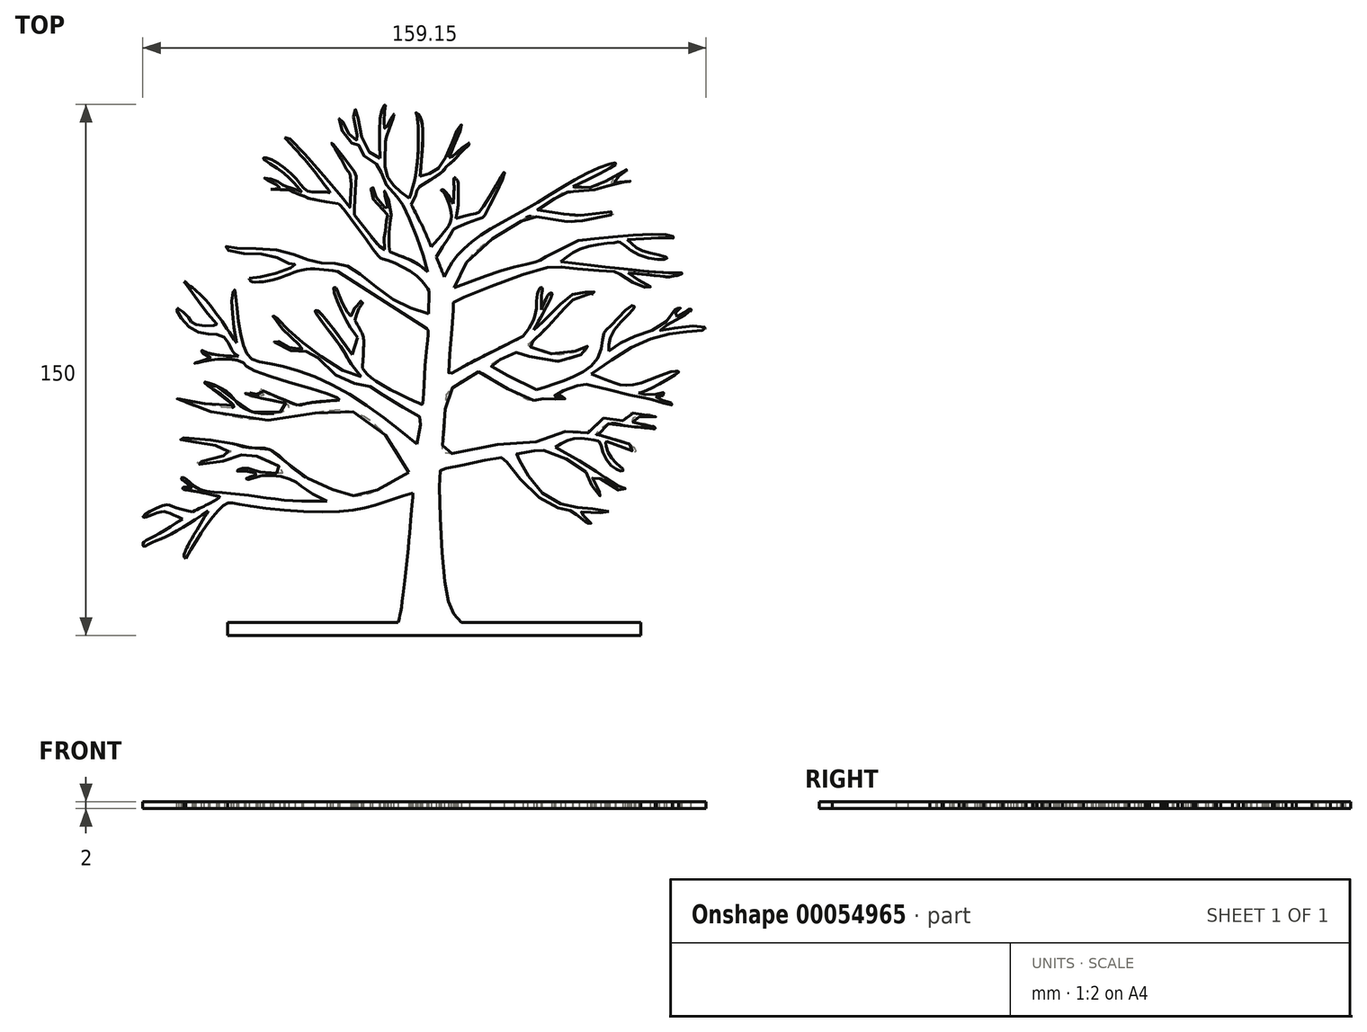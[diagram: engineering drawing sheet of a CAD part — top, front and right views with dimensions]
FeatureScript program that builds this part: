
annotation { "Feature Type Name" : "Feature", "Feature Type Description" : "" }
export const myFeature = defineFeature(function(context is Context, id is Id, definition is map)
    precondition{}
    {
        {
            var Q0;
            Q0=qCreatedBy(makeId("Top.planeOp"),FACE);
            var sketch = newSketch(context, id + "F0", { "sketchPlane" : qUnion([Q0])});
            skFitSpline(sketch, "E0", {"points": [v(-10.21, -68.81) * mm, v(-9.37, -65.06) * mm, v(-6.85, -42.52) * mm, v(-6.02, -32.17) * mm], "startDerivative": vector(3.97, 13.71) * mm, "endDerivative": vector(1.9, 26.28) * mm});
            skFitSpline(sketch, "E1", {"points": [v(-6.02, -32.17) * mm, v(-14.74, -35.01) * mm, v(-27.66, -37.49) * mm, v(-54.51, -35.53) * mm, v(-58.1, -35.01) * mm, v(-60.6, -36.76) * mm, v(-65.35, -42.8) * mm, v(-70.21, -50.73) * mm], "startDerivative": vector(-61.25, -20.1) * mm, "endDerivative": vector(-32.79, -56.2) * mm});
            skFitSpline(sketch, "E2", {"points": [v(-70.21, -50.73) * mm, v(-70.69, -50.15) * mm, v(-63.82, -37.26) * mm], "startDerivative": vector(-3.59, 1.97) * mm, "endDerivative": vector(12.9, 20.96) * mm});
            skFitSpline(sketch, "E3", {"points": [v(-63.82, -37.26) * mm, v(-74.43, -43.86) * mm, v(-80.19, -46.45) * mm, v(-82.14, -47.24) * mm, v(-82.25, -46.4) * mm, v(-79.66, -44.7) * mm, v(-71.1, -39.59) * mm], "startDerivative": vector(-42.12, -28.38) * mm, "endDerivative": vector(39.65, 25.02) * mm});
            skFitSpline(sketch, "E4", {"points": [v(-71.1, -39.59) * mm, v(-75.12, -37.8) * mm, v(-76.86, -37.53) * mm, v(-80.61, -38.69) * mm, v(-81.77, -39.11) * mm, v(-82.25, -38.9) * mm, v(-76.18, -35.63) * mm, v(-73.96, -36.05) * mm, v(-68.31, -37.53) * mm], "startDerivative": vector(-29.89, 13.9) * mm, "endDerivative": vector(37.9, -8.18) * mm});
            skFitSpline(sketch, "E5", {"points": [v(-68.31, -37.53) * mm, v(-60.65, -33.25) * mm, v(-61.34, -33.04) * mm], "startDerivative": vector(14.87, 7.27) * mm, "endDerivative": vector(-4.52, 0.44) * mm});
            skFitSpline(sketch, "E6", {"points": [v(-61.34, -33.04) * mm, v(-67.57, -31.72) * mm, v(-70.95, -31.2) * mm], "startDerivative": vector(-11.6, 2.59) * mm, "endDerivative": vector(-7.4, 1.03) * mm});
            skFitSpline(sketch, "E7", {"points": [v(-70.95, -31.2) * mm, v(-70.95, -30.66) * mm, v(-68.42, -30.77) * mm], "startDerivative": vector(-0.58, 1.97) * mm, "endDerivative": vector(4.96, -0.79) * mm});
            skFitSpline(sketch, "E8", {"points": [v(-68.42, -30.77) * mm, v(-71.4, -27.91) * mm, v(-70.6, -27.87) * mm, v(-67.1, -30.77) * mm, v(-56.96, -32.35) * mm, v(-43.07, -34.15) * mm, v(-30.3, -34.57) * mm], "startDerivative": vector(-35.84, 33.17) * mm, "endDerivative": vector(52.6, 0.18) * mm});
            skFitSpline(sketch, "E9", {"points": [v(-30.3, -34.57) * mm, v(-36.13, -31.33) * mm, v(-39.86, -28.69) * mm, v(-48.85, -27.33) * mm, v(-52.94, -28.36) * mm, v(-53.06, -28.02) * mm, v(-50.3, -27.02) * mm, v(-53.27, -26.05) * mm, v(-55.7, -26.01) * mm, v(-55.45, -25.72) * mm, v(-53.14, -25.22) * mm, v(-49.27, -26.31) * mm], "startDerivative": vector(-47.94, 23.7) * mm, "endDerivative": vector(38.86, -13.3) * mm});
            skFitSpline(sketch, "E10", {"points": [v(-49.27, -26.31) * mm, v(-46.74, -26.35) * mm, v(-42.38, -26.31) * mm, v(-47.57, -22.53) * mm, v(-51.93, -21.7) * mm, v(-55.12, -21.53) * mm, v(-60.48, -23.41) * mm, v(-66.93, -24.04) * mm, v(-67.27, -23.8) * mm, v(-66.77, -23.5) * mm, v(-61.57, -22.4) * mm, v(-57.34, -20.48) * mm, v(-58.1, -20.4) * mm, v(-59.14, -19.9) * mm, v(-62.91, -18.47) * mm, v(-68.06, -17.84) * mm, v(-71.33, -17.25) * mm, v(-72.09, -16.88) * mm, v(-72, -16.46) * mm, v(-71.12, -16.5) * mm, v(-61.74, -17.34) * mm, v(-56.29, -18.47) * mm, v(-51.89, -19.43) * mm, v(-46.57, -19.9) * mm, v(-41.83, -23.54) * mm, v(-34.08, -28.99) * mm, v(-25.83, -32.17) * mm, v(-20.38, -32.89) * mm, v(-7.18, -26.34) * mm], "startDerivative": vector(66.46, 23.55) * mm, "endDerivative": vector(214.35, 130.31) * mm});
            skFitSpline(sketch, "E11", {"points": [v(-7.18, -26.34) * mm, v(-23.22, -9.2) * mm, v(-50.68, -11.54) * mm, v(-72.4, -5.4) * mm, v(-56.58, -7.78) * mm, v(-64.95, -1) * mm, v(-58.66, -3.55) * mm, v(-55.26, -7.18) * mm, v(-47.65, -9.86) * mm, v(-40.93, -7.9) * mm, v(-46.68, -5.65) * mm, v(-52.16, -4.92) * mm, v(-53.51, -3.83) * mm, v(-50.42, -4.28) * mm, v(-48.15, -4.43) * mm, v(-49.1, -3.6) * mm, v(-49.67, -2.48) * mm, v(-46.75, -4.28) * mm, v(-42.82, -5.7) * mm, v(-38.61, -7.37) * mm, v(-36.22, -6.94) * mm, v(-26.74, -6) * mm], "startDerivative": vector(-116.92, 253.36) * mm, "endDerivative": vector(202.88, 11.26) * mm});
            skFitSpline(sketch, "E12", {"points": [v(-26.74, -6) * mm, v(-27.4, -5.29) * mm, v(-51.95, 2.9) * mm, v(-54.07, 4.7) * mm, v(-60.8, 5.62) * mm, v(-67.64, 4.5) * mm, v(-63.32, 6.09) * mm, v(-64.92, 6.89) * mm, v(-65.71, 8.02) * mm, v(-64.38, 7.49) * mm, v(-55.34, 6.35) * mm], "startDerivative": vector(-3.14, 13.4) * mm, "endDerivative": vector(77.7, -4.3) * mm});
            skFitSpline(sketch, "E13", {"points": [v(-55.34, 6.35) * mm, v(-56.87, 7.68) * mm, v(-59.8, 12.08) * mm, v(-67.84, 13.74) * mm, v(-72.7, 20) * mm, v(-69.57, 17.53) * mm, v(-67.64, 15.47) * mm, v(-61.52, 15.33) * mm, v(-61.99, 16.13) * mm, v(-70.7, 27.64) * mm], "startDerivative": vector(-22.53, 12.79) * mm, "endDerivative": vector(-57, 78.87) * mm});
            skFitSpline(sketch, "E14", {"points": [v(-70.7, 27.64) * mm, v(-64.72, 22.45) * mm, v(-55.87, 10.21) * mm], "startDerivative": vector(14.04, -10.51) * mm, "endDerivative": vector(15.55, -23.64) * mm});
            skFitSpline(sketch, "E15", {"points": [v(-55.87, 10.21) * mm, v(-57.13, 22.92) * mm, v(-56.47, 25.31) * mm, v(-55.87, 21.12) * mm, v(-54.07, 10.21) * mm, v(-51.75, 5.82) * mm, v(-46.56, 4.36) * mm, v(-29, -1.5) * mm, v(-4.85, -18.32) * mm], "startDerivative": vector(-16.04, 99.74) * mm, "endDerivative": vector(109.24, -87.43) * mm});
            skFitSpline(sketch, "E16", {"points": [v(-4.85, -18.32) * mm, v(-3.65, -11.34) * mm, v(-3.92, -10.8) * mm, v(-13.16, -5.49) * mm, v(-18.62, -1.96) * mm, v(-26.2, 0) * mm, v(-35.07, 7.69) * mm, v(-38.26, 7.49) * mm, v(-45.3, 10.68) * mm, v(-44.51, 10.88) * mm, v(-43.51, 10.28) * mm, v(-39.06, 8.35) * mm, v(-36.93, 8.69) * mm, v(-37.93, 9.48) * mm, v(-45.3, 17.17) * mm, v(-45.5, 17.97) * mm, v(-44.44, 17.17) * mm, v(-40.63, 13.31) * mm, v(-31.61, 6.16) * mm, v(-20.61, 0.7) * mm], "startDerivative": vector(23.47, 124.9) * mm, "endDerivative": vector(98.14, 5.97) * mm});
            skFitSpline(sketch, "E17", {"points": [v(-20.61, 0.7) * mm, v(-24.2, 5.42) * mm, v(-26, 8.55) * mm, v(-33.59, 18.93) * mm, v(-33.59, 19.33) * mm, v(-32.99, 19.26) * mm, v(-23.14, 6.89) * mm], "startDerivative": vector(-23.28, 28.66) * mm, "endDerivative": vector(41.77, -57.86) * mm});
            skFitSpline(sketch, "E18", {"points": [v(-23.14, 6.89) * mm, v(-21.61, 11.68) * mm], "startDerivative": vector(1.53, 4.79) * mm, "endDerivative": vector(1.53, 4.79) * mm});
            skFitSpline(sketch, "E19", {"points": [v(-21.61, 11.68) * mm, v(-25, 16.86) * mm, v(-28.4, 25.84) * mm, v(-27.8, 25.84) * mm, v(-27.27, 24.65) * mm, v(-23.54, 17.86) * mm, v(-22.63, 19.86) * mm, v(-21.61, 20.79) * mm, v(-20.81, 22.05) * mm, v(-20.22, 21.52) * mm, v(-20.81, 20.66) * mm, v(-22.42, 16.53) * mm], "startDerivative": vector(-22.32, 29) * mm, "endDerivative": vector(-12.72, -43.1) * mm});
            skFitSpline(sketch, "E20", {"points": [v(-22.42, 16.53) * mm, v(-20.31, 12.68) * mm, v(-19.93, 10.55) * mm, v(-20.31, 3.05) * mm], "startDerivative": vector(7.63, -12.78) * mm, "endDerivative": vector(-1.42, -20.17) * mm});
            skFitSpline(sketch, "E21", {"points": [v(-20.31, 3.05) * mm, v(-16.12, -0.8) * mm, v(-3.6, -7.13) * mm, v(-3.26, -6.96) * mm, v(-2.25, 7.83) * mm, v(-2.12, 14.29) * mm], "startDerivative": vector(15.8, -20) * mm, "endDerivative": vector(-12.14, 4.1) * mm});
            skFitSpline(sketch, "E22", {"points": [v(-52.28, 28.5) * mm, v(-48.13, 28.97) * mm, v(-40.94, 31.23) * mm, v(-39.2, 32.07) * mm, v(-39.65, 32.56) * mm, v(-40.85, 32.6) * mm, v(-45.69, 34.83) * mm, v(-54.03, 35.45) * mm, v(-59, 36.87) * mm, v(-59, 37.4) * mm, v(-56.52, 37.05) * mm, v(-45.24, 36.6) * mm, v(-37.07, 34.2) * mm, v(-31.48, 32.78) * mm, v(-26.33, 32.52) * mm, v(-21.27, 29.94) * mm, v(-11.5, 22.48) * mm, v(-1.65, 18.49) * mm], "startDerivative": vector(66.06, 8.87) * mm, "endDerivative": vector(114.77, -35.11) * mm});
            skLineSegment(sketch, "E23", {"start": v(-10.21, -68.81) * mm, "end": v(7.61, -68.81) * mm});
            skLineSegment(sketch, "E24", {"start": v(-27.3, 30.4) * mm, "end": v(-2.12, 14.29) * mm});
            skFitSpline(sketch, "E25", {"points": [v(-1.65, 18.49) * mm, v(-1.45, 24.39) * mm, v(-1.47, 24.8) * mm, v(-1.82, 25.43) * mm, v(-5.7, 29.72) * mm, v(-14.62, 34.02) * mm, v(-15.6, 34.58) * mm, v(-26.86, 49.48) * mm, v(-27.16, 49.55) * mm], "startDerivative": vector(1.62, 48.58) * mm, "endDerivative": vector(-5.15, -2.9) * mm});
            skFitSpline(sketch, "E26", {"points": [v(-27.16, 49.55) * mm, v(-35.09, 50.95) * mm, v(-35.73, 51.15) * mm, v(-36.52, 51.58) * mm, v(-37.54, 51.94) * mm, v(-40.76, 53.37) * mm, v(-41.14, 53.43) * mm, v(-46.15, 53.65) * mm, v(-43.56, 54.09) * mm, v(-47.97, 56.7) * mm, v(-44.87, 56.11) * mm, v(-42.36, 54.6) * mm, v(-40.3, 54.03) * mm, v(-37.47, 52.89) * mm], "startDerivative": vector(-75.54, 13.06) * mm, "endDerivative": vector(34.7, -16.07) * mm});
            skFitSpline(sketch, "E27", {"points": [v(-37.47, 52.89) * mm, v(-38.58, 54.3) * mm, v(-43.27, 58.75) * mm, v(-48.28, 62.44) * mm, v(-46.15, 62.04) * mm, v(-38.77, 56.35) * mm, v(-35.76, 53.08) * mm, v(-32.15, 52.89) * mm, v(-29.37, 52.65) * mm], "startDerivative": vector(-11.68, 15.44) * mm, "endDerivative": vector(25.9, -3.8) * mm});
            skFitSpline(sketch, "E28", {"points": [v(-29.37, 52.65) * mm, v(-34.96, 60.06) * mm, v(-42.23, 68.23) * mm], "startDerivative": vector(-11.1, 15.38) * mm, "endDerivative": vector(-14.57, 15.77) * mm});
            skFitSpline(sketch, "E29", {"points": [v(-42.23, 68.23) * mm, v(-41.28, 68.23) * mm, v(-23.87, 48.52) * mm, v(-23.83, 48.48) * mm, v(-23.61, 57.44) * mm, v(-24.36, 58.75) * mm, v(-27.67, 64.62) * mm, v(-29.03, 66.72) * mm, v(-29.13, 67.02) * mm, v(-22.16, 58.1) * mm, v(-22, 57.64) * mm, v(-22.6, 46.71) * mm, v(-22.5, 46.36) * mm, v(-16.09, 38.18) * mm, v(-14.08, 36.58) * mm], "startDerivative": vector(16.33, 15.47) * mm, "endDerivative": vector(27.04, -14.44) * mm});
            skFitSpline(sketch, "E30", {"points": [v(-27.3, 30.4) * mm, v(-36.46, 30.94) * mm, v(-44.8, 28.26) * mm, v(-51.7, 27.62) * mm, v(-52.28, 28.5) * mm], "startDerivative": vector(-30.11, 4.82) * mm, "endDerivative": vector(-2.56, 9.45) * mm});
            skFitSpline(sketch, "E31", {"points": [v(-14.08, 36.58) * mm, v(-14.08, 40.86) * mm, v(-13.72, 42.16) * mm, v(-13.38, 46) * mm, v(-13.17, 46.35) * mm, v(-13.87, 47.23) * mm, v(-17.94, 52.2) * mm, v(-17.5, 54.38) * mm, v(-17.33, 54.38) * mm, v(-17.18, 52.9) * mm, v(-13.47, 48.07) * mm, v(-13.13, 47.99) * mm, v(-13.97, 51.83) * mm, v(-14.14, 53.21) * mm, v(-13.4, 52.17) * mm, v(-12.13, 45.8) * mm, v(-12.28, 45.5) * mm, v(-12.84, 40.36) * mm, v(-12.7, 36.1) * mm, v(-12.56, 35.96) * mm, v(-10.52, 35.13) * mm, v(-5.24, 32.9) * mm, v(-1.89, 30.28) * mm], "startDerivative": vector(-4.06, 81.98) * mm, "endDerivative": vector(47.57, -44.67) * mm});
            skFitSpline(sketch, "E32", {"points": [v(-1.89, 30.28) * mm, v(-4.65, 39.4) * mm, v(-8.63, 48.68) * mm, v(-10.13, 51.04) * mm, v(-14.63, 56.78) * mm, v(-15.3, 59.78) * mm, v(-20.1, 63.44) * mm, v(-21.47, 66.3) * mm, v(-23.5, 66.84) * mm, v(-26.9, 72.73) * mm, v(-26.6, 73.85) * mm, v(-25.53, 71.96) * mm, v(-22.8, 67.9) * mm, v(-21.63, 67.53) * mm, v(-21.71, 68.52) * mm, v(-22.81, 76.02) * mm, v(-22.29, 76.23) * mm, v(-21.77, 75) * mm, v(-19.33, 65.4) * mm, v(-15.26, 62.42) * mm], "startDerivative": vector(-28.5, 105.1) * mm, "endDerivative": vector(75.49, -28.96) * mm});
            skFitSpline(sketch, "E33", {"points": [v(-15.26, 62.42) * mm, v(-14.8, 76.02) * mm, v(-13.84, 77.57) * mm, v(-13.96, 76.02) * mm, v(-13.84, 70.71) * mm, v(-11.7, 74.6) * mm, v(-11.33, 74.77) * mm, v(-13.66, 68.03) * mm, v(-13.78, 66.48) * mm, v(-13.48, 58.01) * mm, v(-7.04, 51.1) * mm], "startDerivative": vector(-3.61, 94.5) * mm, "endDerivative": vector(56.5, -39.34) * mm});
            skFitSpline(sketch, "E34", {"points": [v(-7.04, 51.1) * mm, v(-4.83, 60.75) * mm, v(-5, 74.95) * mm, v(-5.19, 75.3) * mm, v(-4.06, 74.23) * mm, v(-4.06, 57.35) * mm], "startDerivative": vector(10.87, 32.93) * mm, "endDerivative": vector(-6.74, -67.77) * mm});
            skFitSpline(sketch, "E35", {"points": [v(-4.06, 57.35) * mm, v(1.79, 60.22) * mm, v(6.92, 71.13) * mm, v(7.81, 71.73) * mm, v(4.24, 62.54) * mm, v(4.47, 62.36) * mm, v(9.66, 66.72) * mm, v(10.02, 66.48) * mm, v(9.07, 65.59) * mm, v(4.3, 60.75) * mm, v(3.7, 60.52) * mm, v(2.62, 58.9) * mm, v(-4.77, 53.78) * mm, v(-4.9, 53.06) * mm, v(-6.5, 49.3) * mm], "startDerivative": vector(63.62, 11.93) * mm, "endDerivative": vector(-30.11, -58.53) * mm});
            skFitSpline(sketch, "E36", {"points": [v(-6.5, 49.3) * mm, v(-3.13, 42.64) * mm, v(-0.87, 37.38) * mm], "startDerivative": vector(6.73, -12.83) * mm, "endDerivative": vector(4.48, -10.98) * mm});
            skFitSpline(sketch, "E37", {"points": [v(-0.87, 37.38) * mm, v(3.94, 43.16) * mm, v(4.76, 47.22) * mm, v(2.43, 53) * mm, v(1.98, 53.3) * mm, v(2.36, 53.53) * mm, v(5.37, 49.55) * mm], "startDerivative": vector(22.46, 24.31) * mm, "endDerivative": vector(16.88, -28.84) * mm});
            skFitSpline(sketch, "E38", {"points": [v(5.37, 49.55) * mm, v(5.58, 54.8) * mm, v(5.7, 56.93) * mm, v(6.7, 55.86) * mm], "startDerivative": vector(0.83, 11.66) * mm, "endDerivative": vector(5.05, -6.97) * mm});
            skFitSpline(sketch, "E39", {"points": [v(6.7, 55.86) * mm, v(6.7, 48.85) * mm, v(6.09, 45.33) * mm], "startDerivative": vector(0.43, -13.05) * mm, "endDerivative": vector(-1.8, -7.7) * mm});
            skFitSpline(sketch, "E40", {"points": [v(6.09, 45.33) * mm, v(11.44, 46.77) * mm, v(12.99, 47.61) * mm, v(19.32, 58) * mm, v(19.68, 58.42) * mm, v(19.88, 58.3) * mm, v(13.94, 45.78) * mm, v(13.55, 45.59) * mm, v(5.64, 42.46) * mm, v(5.33, 42.12) * mm, v(0.56, 34.5) * mm], "startDerivative": vector(52.36, 15.08) * mm, "endDerivative": vector(-42.77, -66.51) * mm});
            skFitSpline(sketch, "E41", {"points": [v(0.56, 34.5) * mm, v(2.1, 30.73) * mm, v(2.82, 28.92) * mm], "startDerivative": vector(2.86, -6.96) * mm, "endDerivative": vector(1.58, -4.02) * mm});
            skFitSpline(sketch, "E42", {"points": [v(2.82, 28.92) * mm, v(6.1, 34.4) * mm, v(13.66, 41.04) * mm, v(27.68, 49) * mm, v(44.34, 58.76) * mm, v(51.36, 61.04) * mm, v(51.2, 60.67) * mm, v(39.14, 54.4) * mm], "startDerivative": vector(23.38, 45.86) * mm, "endDerivative": vector(-94.21, -45.05) * mm});
            skFitSpline(sketch, "E43", {"points": [v(39.14, 54.4) * mm, v(39.35, 54) * mm, v(46.92, 54.8) * mm, v(48.4, 55.94) * mm, v(54.97, 59.34) * mm, v(55.34, 59.26) * mm, v(49.8, 55.7) * mm, v(49.92, 55.41) * mm, v(53.27, 55.94) * mm, v(55.5, 55.84) * mm, v(55.5, 55.6) * mm, v(53.22, 55.52) * mm, v(49.98, 54.7) * mm, v(47.74, 54.4) * mm, v(45.06, 53.45) * mm, v(36.7, 52.7) * mm, v(35.76, 52.17) * mm, v(29.12, 47.95) * mm, v(29.68, 47.79) * mm, v(39.99, 46.03) * mm, v(40.89, 46.2) * mm, v(51.04, 47.12) * mm, v(51.12, 46.6) * mm, v(49.76, 46.35) * mm, v(39.56, 44.28) * mm, v(38.4, 44.33) * mm, v(27.34, 46) * mm, v(25.03, 44.97) * mm, v(11.66, 35.96) * mm, v(5.63, 25.84) * mm], "startDerivative": vector(-2.17, -37.4) * mm, "endDerivative": vector(-62.18, -165.42) * mm});
            skFitSpline(sketch, "E44", {"points": [v(5.63, 25.84) * mm, v(22.2, 31.53) * mm, v(29.2, 33.22) * mm, v(30.85, 34.16) * mm, v(40.32, 38.97) * mm, v(41.67, 39.31) * mm, v(62.07, 40.93) * mm, v(67.7, 40.14) * mm, v(67.63, 39.87) * mm, v(66.73, 39.91) * mm, v(54.56, 39.39) * mm], "startDerivative": vector(103.06, 38.8) * mm, "endDerivative": vector(-108.97, -7.39) * mm});
            skFitSpline(sketch, "E45", {"points": [v(54.56, 39.39) * mm, v(58.95, 36.23) * mm, v(65.57, 34.39) * mm, v(65.72, 34.05) * mm, v(58.61, 34.73) * mm, v(52.3, 38.79) * mm, v(51.59, 38.67) * mm, v(43.13, 37.43) * mm, v(35.7, 33.19) * mm], "startDerivative": vector(26.64, -26.8) * mm, "endDerivative": vector(-38.96, -30.57) * mm});
            skFitSpline(sketch, "E46", {"points": [v(35.7, 33.19) * mm, v(67.26, 30) * mm, v(69.81, 30) * mm, v(70, 29.77) * mm, v(66.24, 28.87) * mm, v(65.38, 28.9) * mm, v(54.78, 30.03) * mm], "startDerivative": vector(98.8, -11.95) * mm, "endDerivative": vector(-59.94, 6) * mm});
            skFitSpline(sketch, "E47", {"points": [v(54.78, 30.03) * mm, v(59, 27.17) * mm, v(60.76, 26.39) * mm, v(61.13, 26.12) * mm, v(60.8, 25.82) * mm, v(57.64, 26.54) * mm, v(51.74, 30.03) * mm, v(50.87, 30.33) * mm, v(38.59, 31.35) * mm, v(30.5, 31.2) * mm, v(5.63, 21.76) * mm, v(5.4, 21.43) * mm, v(5.07, 15.75) * mm, v(4.12, 1.12) * mm, v(4.44, 1.3) * mm, v(25.11, 12.08) * mm], "startDerivative": vector(68.6, -50.32) * mm, "endDerivative": vector(202.56, 100.6) * mm});
            skFitSpline(sketch, "E48", {"points": [v(25.11, 12.08) * mm, v(28.7, 18.88) * mm, v(29.12, 24.04) * mm, v(30.18, 25.91) * mm, v(30.47, 25.74) * mm, v(30.33, 24.1) * mm, v(30.25, 19.57) * mm], "startDerivative": vector(20.72, 25.34) * mm, "endDerivative": vector(0.63, -24.43) * mm});
            skFitSpline(sketch, "E49", {"points": [v(30.25, 19.57) * mm, v(32.45, 24.03) * mm, v(33.2, 24.28) * mm, v(33.2, 23.64) * mm, v(28.13, 13.9) * mm], "startDerivative": vector(7.01, 18.49) * mm, "endDerivative": vector(-15.03, -27.06) * mm});
            skFitSpline(sketch, "E50", {"points": [v(28.13, 13.9) * mm, v(30.5, 16.1) * mm, v(38.62, 23.79) * mm, v(39.69, 24) * mm, v(45, 24.89) * mm, v(45.22, 24.74) * mm, v(44.9, 24.1) * mm, v(44.37, 24.1) * mm, v(39.33, 22.47) * mm, v(38.52, 21.9) * mm, v(31.57, 14.25) * mm, v(30.96, 13.9) * mm, v(30.6, 13) * mm, v(26.67, 9.88) * mm, v(26.57, 9.53) * mm, v(36.53, 6.94) * mm, v(43.2, 9.32) * mm, v(43.3, 8.71) * mm, v(36.18, 5.1) * mm, v(23.37, 7.47) * mm, v(23.1, 7.47) * mm, v(16.03, 4.1) * mm, v(16.03, 3.64) * mm, v(28.87, -3.03) * mm], "startDerivative": vector(41, 35.7) * mm, "endDerivative": vector(198.23, -96.55) * mm});
            skFitSpline(sketch, "E51", {"points": [v(28.87, -3.03) * mm, v(37.68, 0) * mm, v(46.17, 5.86) * mm, v(47.87, 12.97) * mm, v(49.35, 14.58) * mm, v(55.78, 20.74) * mm, v(56.5, 20.56) * mm, v(55.92, 19.45) * mm, v(50.1, 12.56) * mm, v(49.35, 7.87) * mm], "startDerivative": vector(57.53, 18.18) * mm, "endDerivative": vector(2.55, -41.47) * mm});
            skFitSpline(sketch, "E52", {"points": [v(49.35, 7.87) * mm, v(55.6, 11.76) * mm, v(64.99, 15.74) * mm, v(68.74, 20.3) * mm, v(69.54, 20.03) * mm, v(68.83, 19.5) * mm, v(67.85, 17.75) * mm, v(70.57, 18.64) * mm, v(72.1, 19.76) * mm, v(72.58, 19.62) * mm, v(71.87, 18.78) * mm, v(63.74, 13.86) * mm, v(68.43, 14.49) * mm, v(76.34, 14.66) * mm, v(76.78, 14.13) * mm, v(71.33, 13.32) * mm, v(59.98, 10.96) * mm, v(44.34, 1.4) * mm], "startDerivative": vector(72.42, 56.3) * mm, "endDerivative": vector(-132.53, -93.7) * mm});
            skFitSpline(sketch, "E53", {"points": [v(44.34, 1.4) * mm, v(48.9, -0.35) * mm, v(55.74, -1.69) * mm, v(67.4, 2.15) * mm, v(69, 2.06) * mm, v(68.96, 1.93) * mm, v(58.55, -3.83) * mm, v(57.7, -3.9) * mm], "startDerivative": vector(29.01, -10.63) * mm, "endDerivative": vector(-6.45, -1.07) * mm});
            skFitSpline(sketch, "E54", {"points": [v(57.7, -3.9) * mm, v(60.26, -4.47) * mm, v(64.29, -3.9) * mm, v(64.97, -3.9) * mm, v(64.77, -4.55) * mm, v(62.76, -5.05) * mm, v(62.74, -5.18) * mm, v(66.27, -6.7) * mm, v(67.03, -6.83) * mm, v(67.23, -7.23) * mm, v(66.5, -7.32) * mm, v(61.2, -5.77) * mm, v(57.97, -5.07) * mm, v(43.87, -1.7) * mm, v(43.04, -1.5) * mm, v(39.24, -2.2) * mm, v(33.99, -4.83) * mm, v(36.73, -4.95) * mm, v(37.02, -5.5) * mm, v(32.56, -5.55) * mm, v(28.08, -6.08) * mm], "startDerivative": vector(43.65, -8.8) * mm, "endDerivative": vector(-58.2, -19.6) * mm});
            skFitSpline(sketch, "E55", {"points": [v(28.08, -6.08) * mm, v(26.83, -6.08) * mm, v(14.13, 1.43) * mm, v(11.74, 1.8) * mm, v(4.05, -3.44) * mm, v(3.21, -6.08) * mm, v(2.5, -18.12) * mm, v(2.14, -20.14) * mm, v(3.21, -21.1) * mm, v(19.44, -18.24) * mm, v(30.9, -17.28) * mm, v(38.76, -14.54) * mm, v(43.42, -15.25) * mm, v(43.63, -14.86) * mm, v(47.6, -11.2) * mm, v(48.45, -11.07) * mm, v(53.14, -11.78) * mm, v(53.46, -11.78) * mm, v(55.42, -9.64) * mm, v(56.1, -9.6) * mm, v(61.32, -10.08) * mm, v(62.84, -10.98) * mm, v(62.21, -11.02) * mm, v(56.45, -10.8) * mm, v(55.96, -11.42) * mm, v(55.82, -12.1) * mm, v(56.23, -12.14) * mm, v(61.63, -13.26) * mm, v(62.44, -13.97) * mm, v(62, -14.02) * mm, v(53, -12.99) * mm, v(48.72, -12.8) * mm, v(45.73, -15.58) * mm, v(46.04, -15.71) * mm, v(54.66, -18.13) * mm, v(56.9, -20.4) * mm, v(56.45, -20.63) * mm, v(55.56, -20.14) * mm, v(48.72, -17.63) * mm], "startDerivative": vector(-50.57, -22.15) * mm, "endDerivative": vector(-218.02, 70.48) * mm});
            skFitSpline(sketch, "E56", {"points": [v(48.72, -17.63) * mm, v(48.4, -17.85) * mm, v(49.72, -21.81) * mm, v(53.06, -25.22) * mm, v(53.34, -25.81) * mm, v(52.92, -26.01) * mm, v(48.96, -23.37) * mm, v(46.65, -17.63) * mm, v(46.14, -17.47) * mm, v(40.62, -16.7) * mm, v(34.23, -19.25) * mm], "startDerivative": vector(-10.24, -2.41) * mm, "endDerivative": vector(-38.2, -23.3) * mm});
            skFitSpline(sketch, "E57", {"points": [v(34.23, -19.25) * mm, v(45.86, -26.13) * mm, v(48.17, -27.8) * mm, v(52.52, -30.43) * mm, v(53.84, -30.85) * mm, v(54.03, -31.28) * mm, v(51.28, -31.14) * mm, v(44.75, -27.16) * mm, v(46.36, -31.56) * mm, v(47.07, -32.46) * mm, v(46.98, -33.03) * mm, v(44.75, -30.62) * mm, v(42.05, -25.4) * mm, v(30.22, -20.06) * mm, v(28.9, -20.2) * mm, v(22.83, -21.38) * mm, v(23.6, -22.38) * mm, v(28.13, -29.72) * mm, v(36.85, -35.63) * mm, v(43.05, -36.53) * mm, v(49.3, -37.38) * mm], "startDerivative": vector(160.83, -92.7) * mm, "endDerivative": vector(104.95, -16.8) * mm});
            skFitSpline(sketch, "E58", {"points": [v(49.3, -37.38) * mm, v(49.3, -37.72) * mm, v(41.1, -37.64) * mm, v(41.33, -38.07) * mm, v(44.21, -40.55) * mm, v(43.99, -41.2) * mm, v(43.11, -40.6) * mm, v(38.87, -37.38) * mm, v(38.47, -37.2) * mm, v(31.16, -34.69) * mm, v(19.94, -22.69) * mm, v(19.05, -22.18) * mm, v(6.76, -24.57) * mm, v(2.07, -25.52) * mm, v(1.7, -26) * mm, v(2.43, -52.17) * mm, v(4.99, -65.48) * mm, v(7.61, -68.81) * mm], "startDerivative": vector(14.78, -23.78) * mm, "endDerivative": vector(49.5, -50.3) * mm});
            skLineSegment(sketch, "E59", {"start": v(0, -68.81) * mm, "end": v(-58.4, -68.81) * mm, "construction": true});
            skLineSegment(sketch, "E60", {"start": v(-58.4, -68.81) * mm, "end": v(-58.4, -72.43) * mm, "construction": true});
            skLineSegment(sketch, "E61", {"start": v(0, 0) * mm, "end": v(0, -89.11) * mm, "construction": true});
            skLineSegment(sketch, "E62.MirrorCS", {"start": v(0, -68.81) * mm, "end": v(58.4, -68.81) * mm, "construction": true});
            skLineSegment(sketch, "E63.bottom", {"start": v(58.4, -68.81) * mm, "end": v(-58.4, -68.81) * mm});
            skLineSegment(sketch, "E63.top", {"start": v(58.4, -72.43) * mm, "end": v(-58.4, -72.43) * mm});
            skLineSegment(sketch, "E63.left", {"start": v(58.4, -68.81) * mm, "end": v(58.4, -72.43) * mm});
            skLineSegment(sketch, "E63.right", {"start": v(-58.4, -68.81) * mm, "end": v(-58.4, -72.43) * mm});
            skSolve(sketch);
        }
        {
            var Q0;
            Q0 = qSketchRegion(id + "F0", true);
            extrude(context, id + "F1", {"entities" : qUnion([Q0]), "depth" : 2 * mm});
        }
    });
